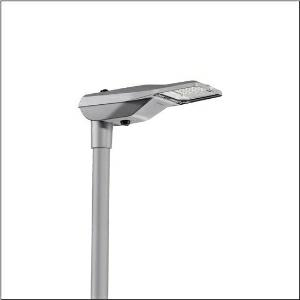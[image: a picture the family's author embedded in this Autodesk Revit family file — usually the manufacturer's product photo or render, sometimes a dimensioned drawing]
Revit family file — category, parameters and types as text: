
# Revit family: streetlight_sl_21_micro___st1_5a_5xe1p43t08db_e62a
name_source: partatom
category: Lighting Fixtures
units: mm (PartAtom-declared; Revit-internal decimal feet)

## family parameters
Cut with Voids When Loaded = No
Host = Face
Light Source = No
Part Type = Normal
Room Calculation Point = No
Round Connector Dimension = Use Diameter
Shared = No

## types (1)
- --- (1 x LED, 5230 lm, 39.1 W, 4000K)
    Apparent Load = 39 VA
    CIE Flux Codes = 22 53 95 100 100
    Color Rendering = 70
    Color Temperature = 4000K
    Default Elevation = 1800 mm
    Description = Streetlight SL 21 micro, mast luminaire, primary light control with lens, of PMMA, primary optical cover: cover, of toughened safety glass, transparent, light distribution: ST1.5a, light emission: direct distribution, primary light characteristic: asymmetric, installation type: side-entry, post-top, LED, High Power LED, rated luminous flux: 5.230lm, luminous efficacy: 134lm/W, light colour: 740, colour temperature: 4000K, control gear: D4i, control: flexible luminous flux parameterisation, time-dependent luminous flux control, constant luminous flux control, overheat protection, pre-setting: logarithmic dimming characteristic, mains connection: 220..240V, AC, 50/60Hz, start of lifetime: 39W, end of service life: 41W, reduction: 18W, luminaire housing, of diecast aluminium, powder-coated, Siteco® metallic grey (DB 702S), corrosivity category C5 mid according to DIN EN ISO 12944, please order mast flange separately, inclination adjustable: 0°, 5°, 10°, 15°, sealing non-destructively replaceable, multi-level sealing system, length: 528mm, width: 235mm, height: 110mm, mast flange for spigot size: 42mm (side-entry): 5XC10008XM4, 60/48mm (side-entry/post-top): 5XC10108XM2, 76/60mm (side-entry/post-top): 5XC10108XM1, Smart Interface below and above, protection rating (complete): IP66, insulation class (complete): insulation class II (safety insulation), certification: CE, ENEC, ENEC+, VDE, impact resistance: IK10, permissible operating ambient temperature for outdoor applications: -40..+50°C, standard-compliant lighting for roads and squares, packaging unit: 1 piece

Light Distribution: ST1.5a
    Height = 110 mm
    Lamp = 1 x LED
    Lamp Light Flux = 5230 lm
    Lamp Power = 39.1 W
    Lamp count = 1
    Length = 528 mm
    Luminous efficacy = 134 lm/W
    Manufacturer = Siteco
    ModVariant = No
    Model = 5XE1P43T08DB
    Number of Poles = 1
    OnlyDefault = Yes
    Power Factor = 1
    Product Name = Streetlight SL 21 micro | ST1.5a
    Product group = mast luminaire | pylon top
    ProductGroupID = 6100
    Protection Class = Protection class II
    Protection Degree = IP 66
    RLX_Detail_Level = 1
    RLX_Emergency_Light_Flux = 0 lm
    RLX_Emergency_Type = 0
    RLX_Emergency_Type_DB = No
    RlxData = <blob elided: 102409 chars, md5=8bec930a>
    Socket = socket
    Standby Power = 0 W
    System Light Flux = 5230 lm
    System Power = 39 W
    Type Comments = factory setting: luminous flux: 100 % | dim-lin: 254 | 765 mA
    Type Image = l_1007239.jpg
    URL = http://relux.com
    VarID = @adj_175115
    Voltage = 0 V
    Weight = 0.00 kg
    Width = 235 mm

## geometry (parser evidence)
native form markers: Blend x4, Sweep x11
no freeform markers — native parametric forms only
